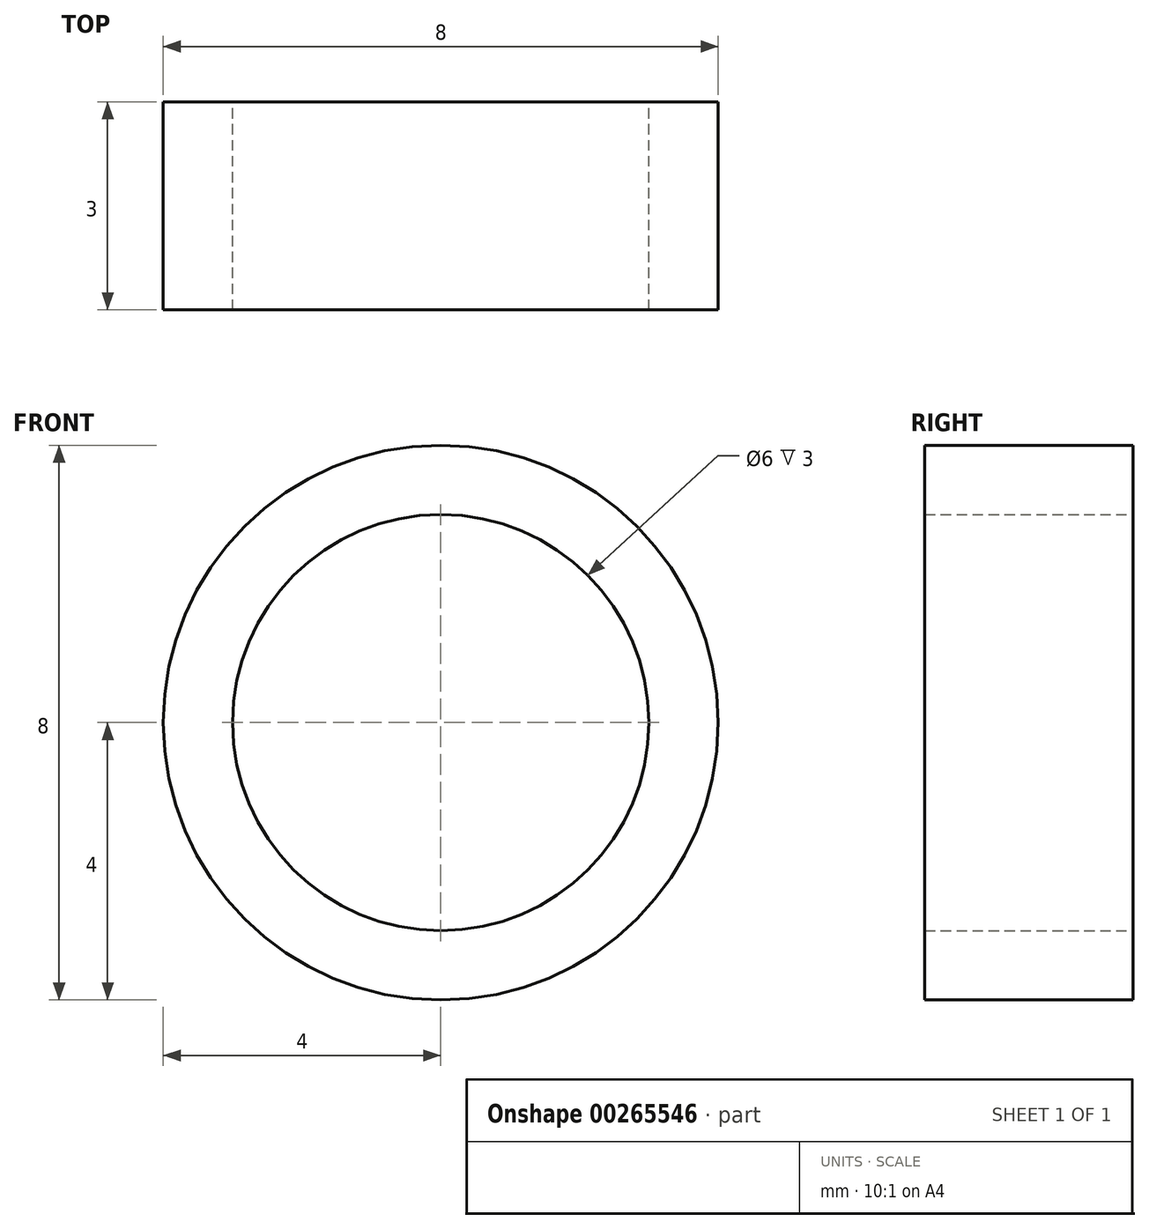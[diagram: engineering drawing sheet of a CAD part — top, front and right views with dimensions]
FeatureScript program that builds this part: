
annotation { "Feature Type Name" : "Feature", "Feature Type Description" : "" }
export const myFeature = defineFeature(function(context is Context, id is Id, definition is map)
    precondition{}
    {
        {
            var Q0;
            Q0=qCreatedBy(makeId("Front.planeOp"),FACE);
            var sketch = newSketch(context, id + "F0", { "sketchPlane" : qUnion([Q0])});
            skCircle(sketch, "E0", {"center": v(0, 0) * mm, "radius": 4 * mm});
            skCircle(sketch, "E1", {"center": v(0, 0) * mm, "radius": 3 * mm});
            skSolve(sketch);
        }
        {
            var Q0;
            Q0=makeQuery(id+"F0.imprint","IMPRINT",FACE,{"disambiguationData":[TD([[makeQuery(id+"F0.imprint","IMPRINT",EDGE,{"derivedFrom":sQuery(id+"F0.wireOp",EDGE,"E0")}),1.0]])]});
            extrude(context, id + "F1", {"entities" : qUnion([Q0]), "depth" : 3 * mm});
        }
    });
